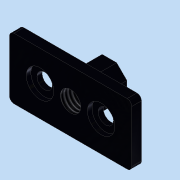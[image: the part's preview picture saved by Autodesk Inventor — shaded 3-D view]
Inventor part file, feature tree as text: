
AUTODESK INVENTOR PART (.ipt)
format: ipt  version: 2013 SP2 (Build 170200200, 200)  size: 125,440 bytes
history: native  units: mm
features: sketch x4, extrude x2, hole x2, fillet x1
ambient origin geometry x8: Origin, YZ Plane, XZ Plane, XY Plane, X Axis, Y Axis, Z Axis, Center Point
bodies: Solid1 (feature_tree)
feature tree (9):
  extrude  "Extrusion1"  Depth=20.0mm
  hole  "Hole1"  [1 undecoded]
  extrude  "Extrusion2"  Depth=10.0mm
  hole  "Hole2"  [1 undecoded]
  fillet  "Fillet1"  Radius=9.5mm
  sketch  "Sketch1"  dims[d0=40.0mm d1=20.0mm]
  sketch  "Sketch2"  dims[d2=3.2mm d3=0.0mm d4=10.0mm]
  sketch  "Sketch3"  dims[d5=20.0mm d6=10.0mm]
  sketch  "Sketch4"  dims[d7=5.0mm d8=6.0mm d9=9.0mm d10=1.5mm d11=90.0deg d12=8.0mm d13=20.594885mm d14=11.48mm d15=9.5mm d16=0.0mm d17=6.647mm d18=20.0mm d19=9.0mm d20=1.5mm d21=90.0deg d22=8.0mm d23=20.594885mm d24=1.5mm]
note: 2 required parameter values undecoded (feature->parameter linkage not recoverable at this tier; creation-order binding heuristic only, values carry confidence <= 0.55)
